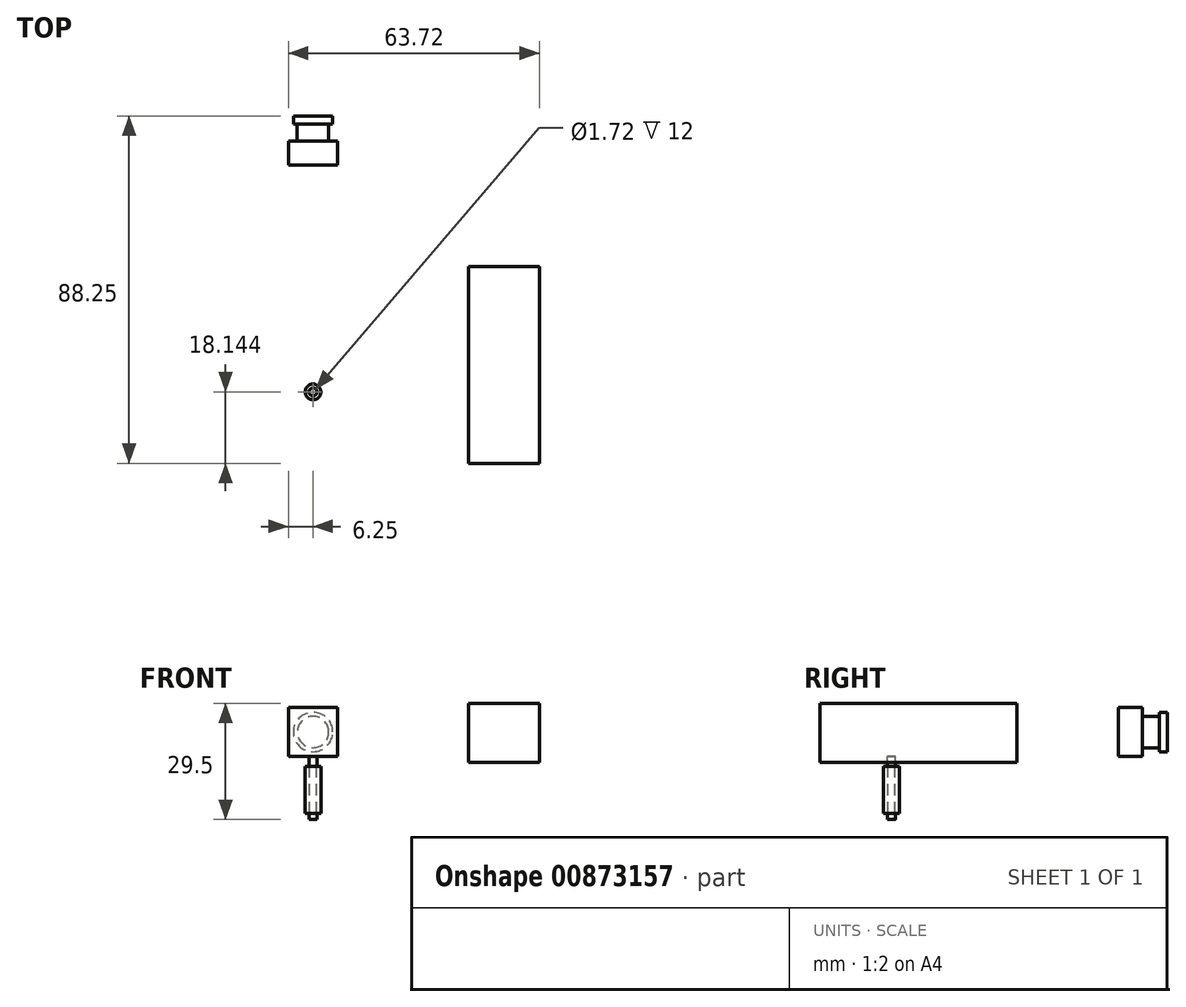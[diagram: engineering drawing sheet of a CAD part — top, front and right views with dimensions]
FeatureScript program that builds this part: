
annotation { "Feature Type Name" : "Feature", "Feature Type Description" : "" }
export const myFeature = defineFeature(function(context is Context, id is Id, definition is map)
    precondition{}
    {
        {
            var Q0;
            Q0=qCreatedBy(makeId("Right.planeOp"),FACE);
            var sketch = newSketch(context, id + "F0", { "sketchPlane" : qUnion([Q0])});
            skLineSegment(sketch, "E0.top", {"start": v(-31.86, 30.06) * mm, "end": v(-33.86, 30.06) * mm});
            skLineSegment(sketch, "E0.left", {"start": v(-31.86, 42.06) * mm, "end": v(-31.86, 30.06) * mm});
            skLineSegment(sketch, "E0.right", {"start": v(-33.86, 42.06) * mm, "end": v(-33.86, 30.06) * mm});
            skLineSegment(sketch, "E1.bottom", {"start": v(-31.86, 30.06) * mm, "end": v(-32.86, 30.06) * mm});
            skLineSegment(sketch, "E1.top", {"start": v(-31.86, 28.56) * mm, "end": v(-32.86, 28.56) * mm});
            skLineSegment(sketch, "E1.left", {"start": v(-31.86, 30.06) * mm, "end": v(-31.86, 28.56) * mm});
            skLineSegment(sketch, "E1.right", {"start": v(-32.86, 30.06) * mm, "end": v(-32.86, 28.56) * mm});
            skLineSegment(sketch, "E2", {"start": v(-31.86, 42.06) * mm, "end": v(-33.86, 42.06) * mm});
            skLineSegment(sketch, "E3", {"start": v(-32.72, 32.33) * mm, "end": v(-32.72, 30.06) * mm});
            skLineSegment(sketch, "E4.bottom", {"start": v(-31.86, 42.06) * mm, "end": v(-32.86, 42.06) * mm});
            skLineSegment(sketch, "E4.top", {"start": v(-31.86, 44.56) * mm, "end": v(-32.86, 44.56) * mm});
            skLineSegment(sketch, "E4.left", {"start": v(-31.86, 42.06) * mm, "end": v(-31.86, 44.56) * mm});
            skLineSegment(sketch, "E4.right", {"start": v(-32.86, 42.06) * mm, "end": v(-32.86, 44.56) * mm});
            skLineSegment(sketch, "E5", {"start": v(-32.72, 30.06) * mm, "end": v(-32.72, 42.06) * mm});
            skSolve(sketch);
        }
        {
            var Q0;
            {var subQ1=sQuery(id+"F0.wireOp",EDGE,"E0.right");Q0=makeQuery(id+"F0.imprint","IMPRINT",FACE,{"disambiguationData":[TD([[makeQuery(id+"F0.imprint","IMPRINT",EDGE,{"derivedFrom":subQ1}),1.0]])]});}
            var Q1;
            Q1=makeQuery(id+"F0.imprint","IMPRINT",FACE,{"disambiguationData":[TD([[makeQuery(id+"F0.imprint","IMPRINT",EDGE,{"derivedFrom":sQuery(id+"F0.wireOp",EDGE,"E1.top")}),-1.0]])]});
            var Q2;
            Q2=makeQuery(id+"F0.imprint","IMPRINT",FACE,{"disambiguationData":[TD([[makeQuery(id+"F0.imprint","IMPRINT",EDGE,{"derivedFrom":sQuery(id+"F0.wireOp",EDGE,"E4.top")}),1.0]])]});
            var Q3;
            Q3=sQuery(id+"F0.wireOp",EDGE,"E0.left");
            revolve(context, id + "F1", {"surfaceOperationType" : NewSurfaceOperationType.NEW, "entities" : qUnion([Q0, Q1, Q2]), "axis" : qUnion([Q3]), "revolveType" : RevolveType.FULL});
        }
        {
            var Q0;
            Q0=qCreatedBy(makeId("Front.planeOp"),FACE);
            var sketch = newSketch(context, id + "F2", { "sketchPlane" : qUnion([Q0])});
            skLineSegment(sketch, "E6.bottom", {"start": v(39.47, 58.06) * mm, "end": v(57.47, 58.06) * mm});
            skLineSegment(sketch, "E6.top", {"start": v(39.47, 43.06) * mm, "end": v(57.47, 43.06) * mm});
            skLineSegment(sketch, "E6.left", {"start": v(39.47, 58.06) * mm, "end": v(39.47, 43.06) * mm});
            skLineSegment(sketch, "E6.right", {"start": v(57.47, 58.06) * mm, "end": v(57.47, 43.06) * mm});
            skSolve(sketch);
        }
        {
            var Q0;
            Q0 = qSketchRegion(id + "F2", true);
            extrude(context, id + "F3", {"entities" : qUnion([Q0]), "depth" : 50 * mm, "offsetDistance" : 25 * mm});
        }
        {
            var Q0;
            Q0=qCreatedBy(makeId("Right.planeOp"),FACE);
            var sketch = newSketch(context, id + "F4", { "sketchPlane" : qUnion([Q0])});
            skLineSegment(sketch, "E7.left", {"start": v(25.75, 57.05) * mm, "end": v(25.75, 44.55) * mm});
            skPoint(sketch, "E8.third.point", {"position": v(38.25, 50.8) * mm});
            skLineSegment(sketch, "E9.bottom", {"start": v(38.25, 50.8) * mm, "end": v(36.25, 50.8) * mm});
            skLineSegment(sketch, "E9.top", {"start": v(38.25, 45.8) * mm, "end": v(36.25, 45.8) * mm});
            skLineSegment(sketch, "E9.left", {"start": v(38.25, 50.8) * mm, "end": v(38.25, 45.8) * mm});
            skLineSegment(sketch, "E9.right", {"start": v(36.25, 50.8) * mm, "end": v(36.25, 45.8) * mm});
            skLineSegment(sketch, "E10.bottom", {"start": v(36.25, 50.8) * mm, "end": v(31.92, 50.8) * mm});
            skLineSegment(sketch, "E10.top", {"start": v(36.25, 46.8) * mm, "end": v(31.92, 46.8) * mm});
            skLineSegment(sketch, "E10.left", {"start": v(36.25, 50.8) * mm, "end": v(36.25, 46.8) * mm});
            skLineSegment(sketch, "E10.right", {"start": v(31.92, 50.8) * mm, "end": v(31.92, 46.8) * mm});
            skPoint(sketch, "E11.oppositeSnap0", {"position": v(32, 44.55) * mm});
            skPoint(sketch, "E11.oppositeSnap1", {"position": v(31.92, 48.8) * mm});
            skLineSegment(sketch, "E11.bottom", {"start": v(25.75, 57.05) * mm, "end": v(31.92, 57.05) * mm});
            skLineSegment(sketch, "E11.top", {"start": v(25.75, 44.55) * mm, "end": v(31.92, 44.55) * mm});
            skLineSegment(sketch, "E11.right", {"start": v(31.92, 57.05) * mm, "end": v(31.92, 44.55) * mm});
            skLineSegment(sketch, "E12", {"start": v(31.92, 50.8) * mm, "end": v(38.25, 50.8) * mm});
            skLineSegment(sketch, "E13", {"start": v(31.92, 50.8) * mm, "end": v(42.65, 50.8) * mm});
            skSolve(sketch);
        }
        {
            var Q0;
            {var subQ1=sQuery(id+"F4.wireOp",EDGE,"E9.bottom");Q0=makeQuery(id+"F4.imprint","IMPRINT",FACE,{"disambiguationData":[TD([[makeQuery(id+"F4.imprint","IMPRINT",EDGE,{"derivedFrom":subQ1}),1.0]])]});}
            var Q1;
            {var subQ0=sQuery(id+"F4.wireOp",EDGE,"E10.bottom");Q1=makeQuery(id+"F4.imprint","IMPRINT",FACE,{"disambiguationData":[TD([[makeQuery(id+"F4.imprint","IMPRINT",EDGE,{"derivedFrom":subQ0}),1.0]])]});}
            var Q2;
            Q2=sQuery(id+"F4.wireOp",EDGE,"E13");
            revolve(context, id + "F5", {"surfaceOperationType" : NewSurfaceOperationType.NEW, "entities" : qUnion([Q0, Q1]), "axis" : qUnion([Q2]), "revolveType" : RevolveType.FULL});
        }
        {
            var Q0;
            Q0=makeQuery(id+"F4.imprint","IMPRINT",FACE,{"disambiguationData":[TD([[makeQuery(id+"F4.imprint","IMPRINT",EDGE,{"derivedFrom":sQuery(id+"F4.wireOp",EDGE,"E7.left")}),1.0]])]});
            extrude(context, id + "F6", {"entities" : qUnion([Q0]), "operationType" : NewBodyOperationType.ADD, "depth" : 6.25 * mm, "offsetDistance" : 25 * mm, "hasSecondDirection" : true, "secondDirectionOppositeDirection" : true, "secondDirectionDepth" : 6.25 * mm});
        }
    });
